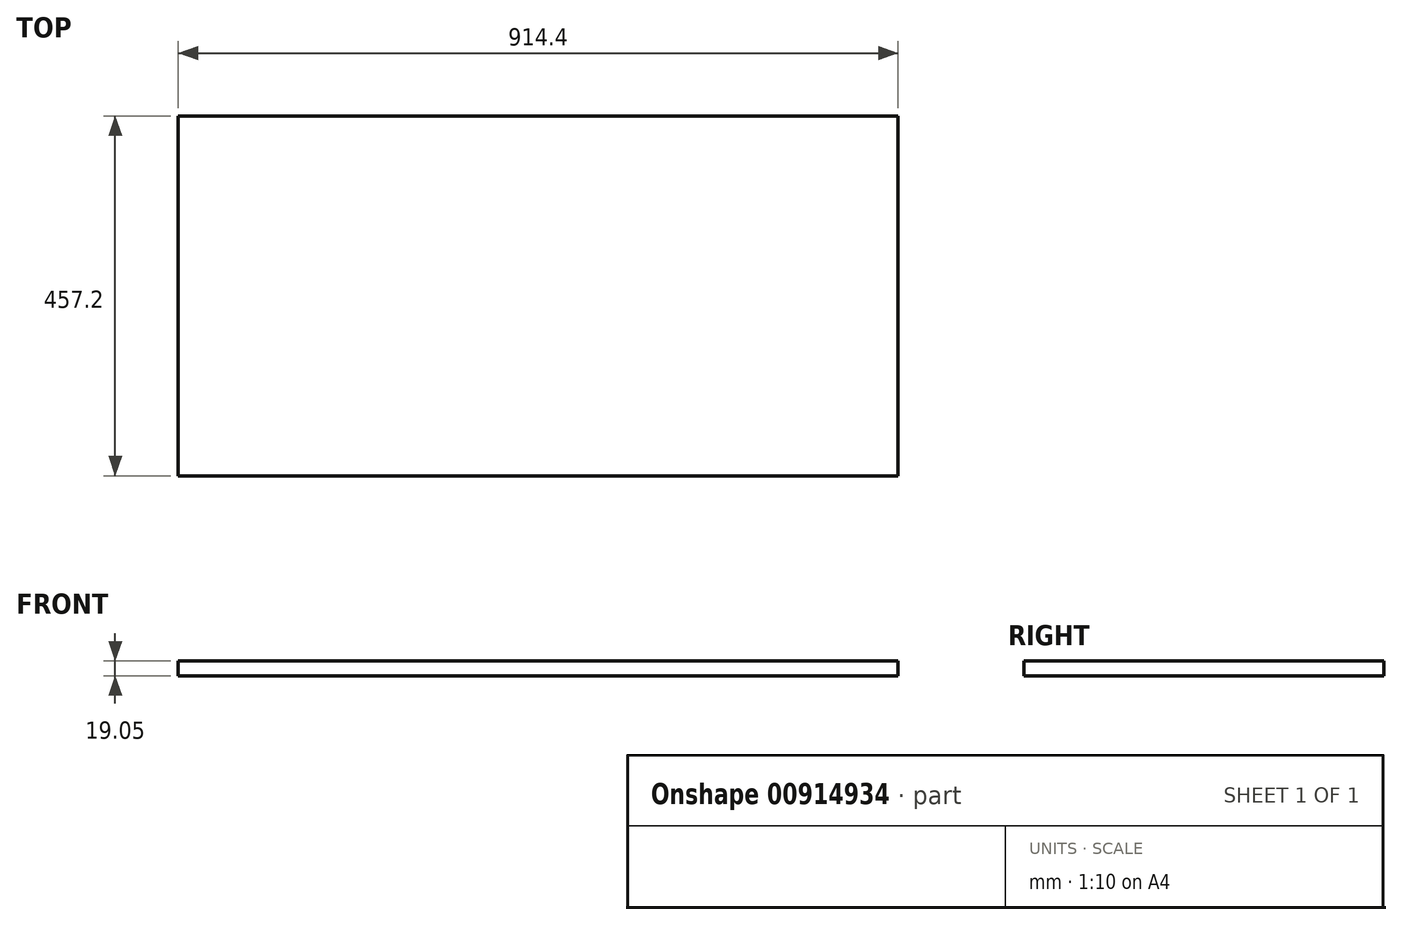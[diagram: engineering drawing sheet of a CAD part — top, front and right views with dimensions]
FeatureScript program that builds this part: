
annotation { "Feature Type Name" : "Feature", "Feature Type Description" : "" }
export const myFeature = defineFeature(function(context is Context, id is Id, definition is map)
    precondition{}
    {
        {
            var Q0;
            Q0=qCreatedBy(makeId("Top.planeOp"),FACE);
            var sketch = newSketch(context, id + "F0", { "sketchPlane" : qUnion([Q0])});
            skLineSegment(sketch, "E0.bottom", {"start": v(-326.7, 21.83) * mm, "end": v(587.7, 21.83) * mm});
            skLineSegment(sketch, "E0.top", {"start": v(-326.7, -435.37) * mm, "end": v(587.7, -435.37) * mm});
            skLineSegment(sketch, "E0.left", {"start": v(-326.7, 21.83) * mm, "end": v(-326.7, -435.37) * mm});
            skLineSegment(sketch, "E0.right", {"start": v(587.7, 21.83) * mm, "end": v(587.7, -435.37) * mm});
            skSolve(sketch);
        }
        {
            var Q0;
            Q0=makeQuery(id+"F0.imprint","IMPRINT",FACE,{"disambiguationData":[TD([[makeQuery(id+"F0.imprint","IMPRINT",EDGE,{"derivedFrom":sQuery(id+"F0.wireOp",EDGE,"E0.bottom")}),-1.0]])]});
            extrude(context, id + "F1", {"entities" : qUnion([Q0]), "oppositeDirection" : true, "depth" : 19.05 * mm, "offsetDistance" : 25.4 * mm});
        }
    });
